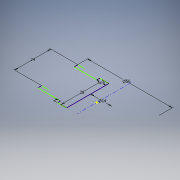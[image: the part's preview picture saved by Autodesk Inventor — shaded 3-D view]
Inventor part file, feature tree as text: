
AUTODESK INVENTOR PART (.ipt)
format: ipt  version: 2018.1 (Build 221171000, 171)  size: 93,696 bytes
history: native  units: mm
features: sketch x1
ambient origin geometry x8: Origin, YZ Plane, XZ Plane, XY Plane, X Axis, Y Axis, Z Axis, Center Point
feature tree (1):
  sketch  "Sketch1"  dims[d2=28.0mm d5=6.0mm d6=56.0mm d8=2.0mm d12=24.0mm]
